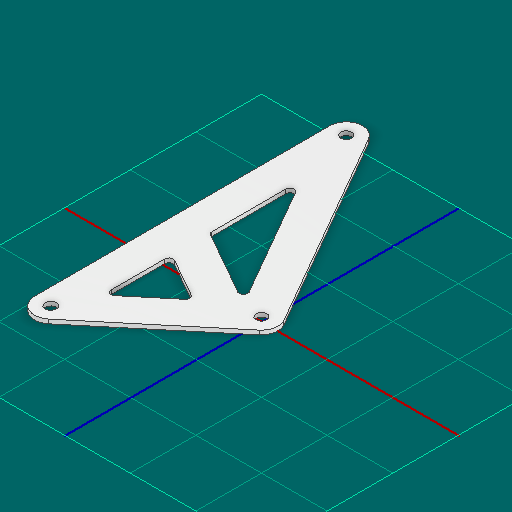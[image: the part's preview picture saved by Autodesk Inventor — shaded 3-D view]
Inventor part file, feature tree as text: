
AUTODESK INVENTOR PART (.ipt)
format: ipt  version: 2025 (Build 290162000, 162)  size: 154,624 bytes
history: native  units: in
note: dims shown in document units (in); Inventor stores cm internally (conversion verified against a paired STEP export)
features: other x5, sketch x1
ambient origin geometry x8: Origin, YZ Plane, XZ Plane, XY Plane, X Axis, Y Axis, Z Axis, Center Point
bodies: Solid1 (feature_tree)
feature tree (6):
  other  "gusset.ipt"
  other  "Blocks"
  other  "main"
  other  "Solid1::gusset.ipt"
  other  "TaggingFeature1"
  sketch  "Sketch1"  dims[d0=0.3937in d1=0.5in d2=0.5in d3=0.5in d4=0.0625in d5=0.5in d6=0.0625in d7=0.0625in d10=4.5in d12=0.5in d13=0.5in d14=0.5192in d16=1.75in d17=0.5in]
